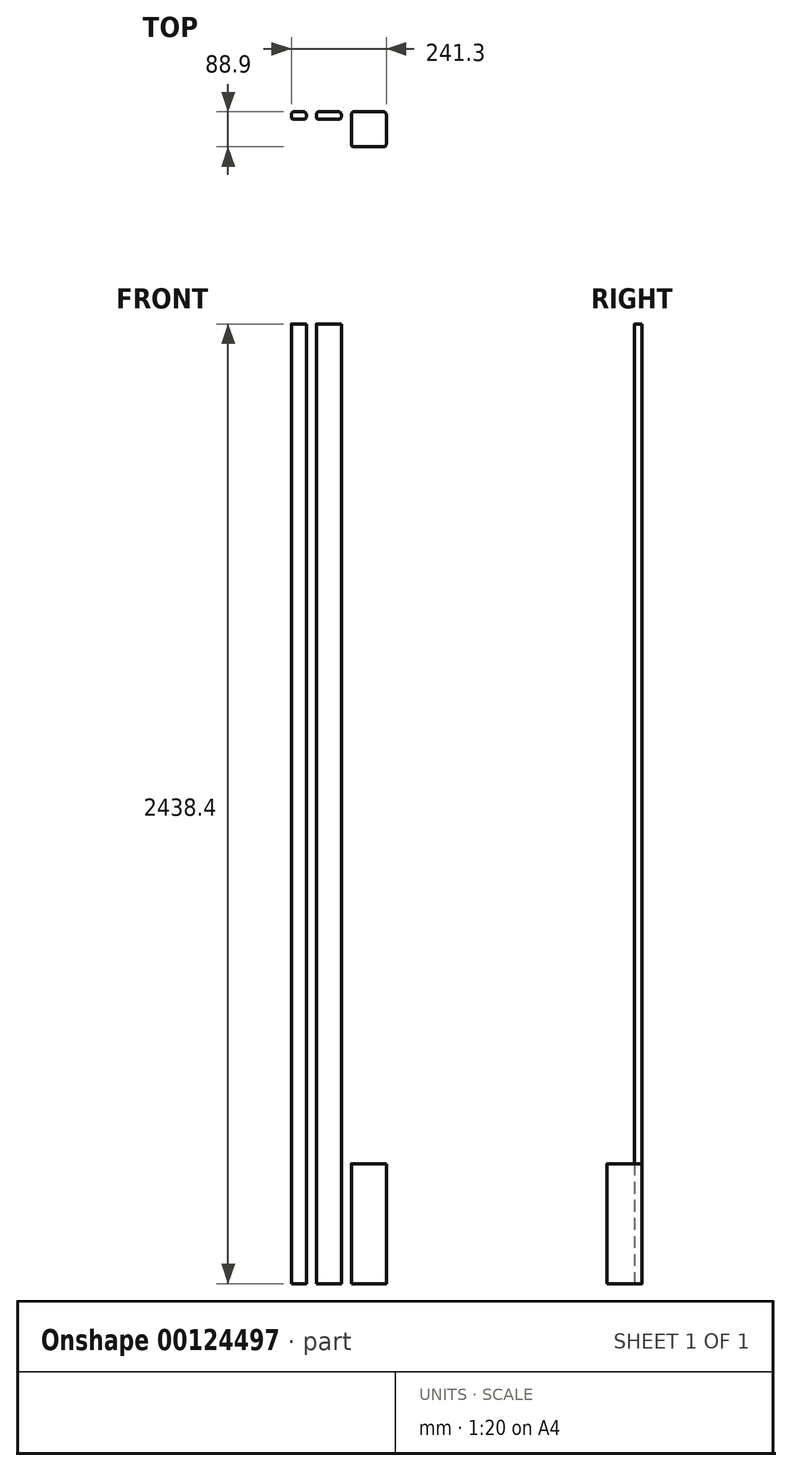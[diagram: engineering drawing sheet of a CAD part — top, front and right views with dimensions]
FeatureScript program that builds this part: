
annotation { "Feature Type Name" : "Feature", "Feature Type Description" : "" }
export const myFeature = defineFeature(function(context is Context, id is Id, definition is map)
    precondition{}
    {
        {
            var Q0;
            Q0=qCreatedBy(makeId("Top.planeOp"),FACE);
            var sketch = newSketch(context, id + "F0", { "sketchPlane" : qUnion([Q0])});
            skLineSegment(sketch, "E0.bottom", {"start": v(6.35, 0) * mm, "end": v(31.75, 0) * mm});
            skLineSegment(sketch, "E0.top", {"start": v(6.35, -19.05) * mm, "end": v(31.75, -19.05) * mm});
            skLineSegment(sketch, "E0.left", {"start": v(0, -6.35) * mm, "end": v(0, -12.7) * mm});
            skLineSegment(sketch, "E0.right", {"start": v(38.1, -6.35) * mm, "end": v(38.1, -12.7) * mm});
            skLineSegment(sketch, "E1.bottom", {"start": v(69.85, 0) * mm, "end": v(120.65, 0) * mm});
            skLineSegment(sketch, "E1.top", {"start": v(69.85, -19.05) * mm, "end": v(120.65, -19.05) * mm});
            skLineSegment(sketch, "E1.left", {"start": v(63.5, -6.35) * mm, "end": v(63.5, -12.7) * mm});
            skLineSegment(sketch, "E1.right", {"start": v(127, -6.35) * mm, "end": v(127, -12.7) * mm});
            skPoint(sketch, "E2.visualSharp", {"position": v(38.1, 0) * mm});
            skArc(sketch, "E2.filletArc", {"start": v(38.1, -6.35) * mm, "mid": v(36.24, -1.86) * mm, "end": v(31.75, 0) * mm});
            skPoint(sketch, "E3.visualSharp", {"position": v(38.1, -19.05) * mm});
            skArc(sketch, "E3.filletArc", {"start": v(31.75, -19.05) * mm, "mid": v(36.24, -17.2) * mm, "end": v(38.1, -12.7) * mm});
            skPoint(sketch, "E4.visualSharp", {"position": v(0, -19.05) * mm});
            skArc(sketch, "E4.filletArc", {"start": v(0, -12.7) * mm, "mid": v(1.86, -17.2) * mm, "end": v(6.35, -19.05) * mm});
            skPoint(sketch, "E5.visualSharp", {"position": v(0, 0) * mm});
            skArc(sketch, "E5.filletArc", {"start": v(6.35, 0) * mm, "mid": v(1.86, -1.86) * mm, "end": v(0, -6.35) * mm});
            skPoint(sketch, "E6.visualSharp", {"position": v(63.5, 0) * mm});
            skArc(sketch, "E6.filletArc", {"start": v(69.85, 0) * mm, "mid": v(65.36, -1.86) * mm, "end": v(63.5, -6.35) * mm});
            skPoint(sketch, "E7.visualSharp", {"position": v(63.5, -19.05) * mm});
            skArc(sketch, "E7.filletArc", {"start": v(63.5, -12.7) * mm, "mid": v(65.36, -17.2) * mm, "end": v(69.85, -19.05) * mm});
            skPoint(sketch, "E8.visualSharp", {"position": v(127, -19.05) * mm});
            skArc(sketch, "E8.filletArc", {"start": v(120.65, -19.05) * mm, "mid": v(125.14, -17.2) * mm, "end": v(127, -12.7) * mm});
            skPoint(sketch, "E9.visualSharp", {"position": v(127, 0) * mm});
            skArc(sketch, "E9.filletArc", {"start": v(127, -6.35) * mm, "mid": v(125.14, -1.86) * mm, "end": v(120.65, 0) * mm});
            skLineSegment(sketch, "E10.bottom", {"start": v(158.75, 0) * mm, "end": v(234.95, 0) * mm});
            skLineSegment(sketch, "E10.top", {"start": v(158.75, -88.9) * mm, "end": v(234.95, -88.9) * mm});
            skLineSegment(sketch, "E10.left", {"start": v(152.4, -6.35) * mm, "end": v(152.4, -82.55) * mm});
            skLineSegment(sketch, "E10.right", {"start": v(241.3, -6.35) * mm, "end": v(241.3, -82.55) * mm});
            skPoint(sketch, "E11.visualSharp", {"position": v(152.4, 0) * mm});
            skArc(sketch, "E11.filletArc", {"start": v(158.75, 0) * mm, "mid": v(154.26, -1.86) * mm, "end": v(152.4, -6.35) * mm});
            skPoint(sketch, "E12.visualSharp", {"position": v(241.3, 0) * mm});
            skArc(sketch, "E12.filletArc", {"start": v(241.3, -6.35) * mm, "mid": v(239.44, -1.86) * mm, "end": v(234.95, 0) * mm});
            skPoint(sketch, "E13.visualSharp", {"position": v(241.3, -88.9) * mm});
            skArc(sketch, "E13.filletArc", {"start": v(234.95, -88.9) * mm, "mid": v(239.44, -87.04) * mm, "end": v(241.3, -82.55) * mm});
            skPoint(sketch, "E14.visualSharp", {"position": v(152.4, -88.9) * mm});
            skArc(sketch, "E14.filletArc", {"start": v(152.4, -82.55) * mm, "mid": v(154.26, -87.04) * mm, "end": v(158.75, -88.9) * mm});
            skSolve(sketch);
        }
        {
            var Q0;
            Q0=makeQuery(id+"F0.imprint","IMPRINT",FACE,{"disambiguationData":[TD([[makeQuery(id+"F0.imprint","IMPRINT",EDGE,{"derivedFrom":sQuery(id+"F0.wireOp",EDGE,"E0.bottom")}),-1.0]])]});
            extrude(context, id + "F1", {"entities" : qUnion([Q0]), "depth" : 2438.4 * mm});
        }
        {
            var Q0;
            Q0=makeQuery(id+"F0.imprint","IMPRINT",FACE,{"disambiguationData":[TD([[makeQuery(id+"F0.imprint","IMPRINT",EDGE,{"derivedFrom":sQuery(id+"F0.wireOp",EDGE,"E1.bottom")}),-1.0]])]});
            extrude(context, id + "F2", {"entities" : qUnion([Q0]), "depth" : 2438.4 * mm});
        }
        {
            var Q0;
            Q0=makeQuery(id+"F0.imprint","IMPRINT",FACE,{"disambiguationData":[TD([[makeQuery(id+"F0.imprint","IMPRINT",EDGE,{"derivedFrom":sQuery(id+"F0.wireOp",EDGE,"E10.bottom")}),-1.0]])]});
            extrude(context, id + "F3", {"entities" : qUnion([Q0]), "depth" : 304.8 * mm});
        }
    });
